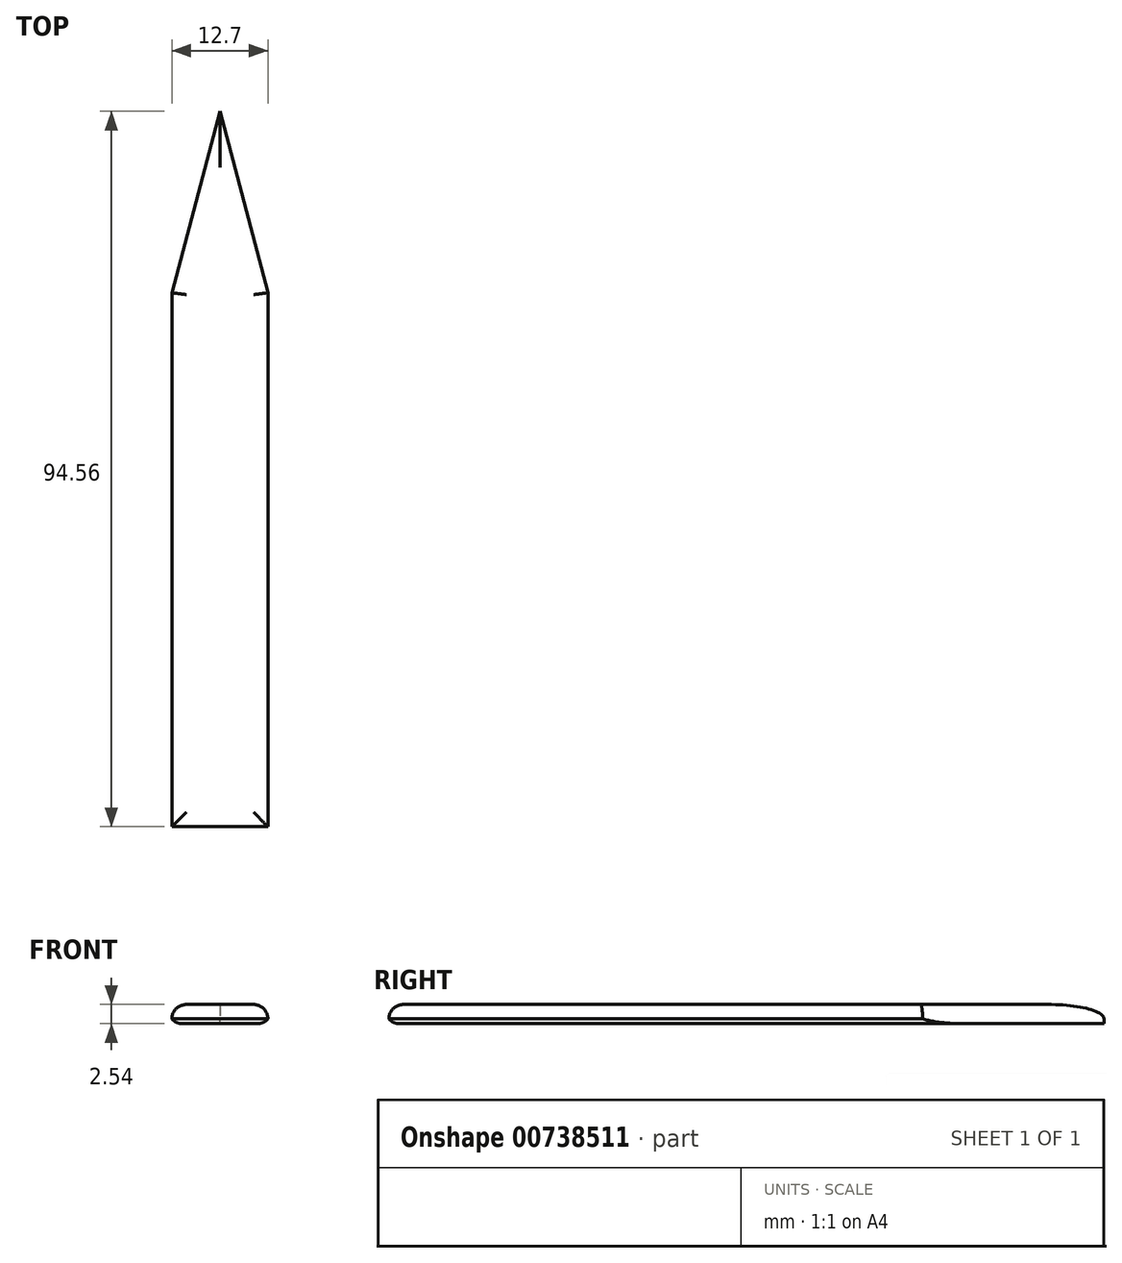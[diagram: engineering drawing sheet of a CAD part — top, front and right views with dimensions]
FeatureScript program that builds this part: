
annotation { "Feature Type Name" : "Feature", "Feature Type Description" : "" }
export const myFeature = defineFeature(function(context is Context, id is Id, definition is map)
    precondition{}
    {
        {
            var Q0;
            Q0=qCreatedBy(makeId("Top.planeOp"),FACE);
            var sketch = newSketch(context, id + "F0", { "sketchPlane" : qUnion([Q0])});
            skLineSegment(sketch, "E0.bottom", {"start": v(-12.7, 41.62) * mm, "end": v(0, 41.62) * mm});
            skLineSegment(sketch, "E0.top", {"start": v(-12.7, -52.94) * mm, "end": v(0, -52.94) * mm});
            skLineSegment(sketch, "E0.left", {"start": v(-12.7, 41.62) * mm, "end": v(-12.7, -52.94) * mm});
            skLineSegment(sketch, "E0.right", {"start": v(0, 41.62) * mm, "end": v(0, -52.94) * mm});
            skSolve(sketch);
        }
        {
            var Q0;
            Q0=makeQuery(id+"F0.imprint","IMPRINT",FACE,{"disambiguationData":[TD([[makeQuery(id+"F0.imprint","IMPRINT",EDGE,{"derivedFrom":sQuery(id+"F0.wireOp",EDGE,"E0.bottom")}),-1.0]])]});
            extrude(context, id + "F1", {"entities" : qUnion([Q0]), "depth" : 2.54 * mm, "offsetDistance" : 25.4 * mm});
        }
        {
            var Q0;
            Q0=makeQuery(id+"F1.opExtrude","CAP_FACE",FACE,{"disambiguationData":[OSD([sQuery(id+"F0.wireOp",EDGE,"E0.bottom"),sQuery(id+"F0.wireOp",EDGE,"E0.top"),sQuery(id+"F0.wireOp",EDGE,"E0.left"),sQuery(id+"F0.wireOp",EDGE,"E0.right")])],"isStart":false});
            var sketch = newSketch(context, id + "F2", { "sketchPlane" : qUnion([Q0])});
            skLineSegment(sketch, "E1", {"start": v(-6.35, 41.62) * mm, "end": v(-12.7, 17.63) * mm});
            skLineSegment(sketch, "E2", {"start": v(-12.7, 17.63) * mm, "end": v(-12.7, 41.62) * mm});
            skLineSegment(sketch, "E3", {"start": v(-12.7, 41.62) * mm, "end": v(-6.35, 41.62) * mm});
            skLineSegment(sketch, "E4", {"start": v(-6.35, 41.62) * mm, "end": v(0, 17.63) * mm});
            skLineSegment(sketch, "E5", {"start": v(0, 17.63) * mm, "end": v(0, 41.62) * mm});
            skLineSegment(sketch, "E6", {"start": v(0, 41.62) * mm, "end": v(-6.35, 41.62) * mm});
            skSolve(sketch);
        }
        {
            var Q0;
            Q0 = qSketchRegion(id + "F2", true);
            extrude(context, id + "F3", {"entities" : qUnion([Q0]), "operationType" : NewBodyOperationType.REMOVE, "oppositeDirection" : true, "depth" : 3.8 * mm, "offsetDistance" : 25.4 * mm});
        }
        {
            var Q0;
            Q0=makeQuery(id+"F3.boolean.opBoolean","COPY",EDGE,{"derivedFrom":makeQuery(id+"F3.opExtrude","CAP_EDGE",EDGE,{"disambiguationData":[OSD([sQuery(id+"F2.wireOp",EDGE,"E4")])],"isStart":true})});
            var Q1;
            Q1=makeQuery(id+"F1.opExtrude","CAP_EDGE",EDGE,{"disambiguationData":[OSD([sQuery(id+"F0.wireOp",EDGE,"E0.left")])],"isStart":false});
            var Q2;
            Q2=makeQuery(id+"F1.opExtrude","CAP_FACE",FACE,{"disambiguationData":[OSD([sQuery(id+"F0.wireOp",EDGE,"E0.bottom"),sQuery(id+"F0.wireOp",EDGE,"E0.top"),sQuery(id+"F0.wireOp",EDGE,"E0.left"),sQuery(id+"F0.wireOp",EDGE,"E0.right")])],"isStart":false});
            fillet(context, id + "F4", {"entities" : qUnion([Q0, Q1, Q2]), "radius" : 1.9 * mm, "tangentPropagation" : true, "allowEdgeOverflow" : false});
        }
        {
            var Q0;
            Q0=makeQuery(id+"F1.opExtrude","CAP_EDGE",EDGE,{"disambiguationData":[OSD([sQuery(id+"F0.wireOp",EDGE,"E0.top")])],"isStart":true});
            var Q1;
            Q1=makeQuery(id+"F1.opExtrude","CAP_EDGE",EDGE,{"disambiguationData":[OSD([sQuery(id+"F0.wireOp",EDGE,"E0.left")])],"isStart":true});
            var Q2;
            Q2=makeQuery(id+"F1.opExtrude","CAP_EDGE",EDGE,{"disambiguationData":[OSD([sQuery(id+"F0.wireOp",EDGE,"E0.right")])],"isStart":true});
            var Q3;
            Q3=makeQuery(id+"F3.boolean.opBoolean","COPY",EDGE,{"derivedFrom":makeQuery(id+"F3.opExtrude","CAP_EDGE",EDGE,{"disambiguationData":[OSD([sQuery(id+"F2.wireOp",EDGE,"E4")])],"isStart":false})});
            var Q4;
            Q4=makeQuery(id+"F3.boolean.opBoolean","COPY",EDGE,{"derivedFrom":makeQuery(id+"F3.opExtrude","CAP_EDGE",EDGE,{"disambiguationData":[OSD([sQuery(id+"F2.wireOp",EDGE,"E1")])],"isStart":false})});
            fillet(context, id + "F5", {"entities" : qUnion([Q0, Q1, Q2, Q3, Q4]), "radius" : 1.9 * mm, "tangentPropagation" : true, "allowEdgeOverflow" : false});
        }
    });
